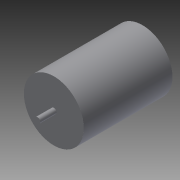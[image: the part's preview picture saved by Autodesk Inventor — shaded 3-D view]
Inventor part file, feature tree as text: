
AUTODESK INVENTOR PART (.ipt)
format: ipt  version: 2015 SP1 (Build 190203100, 203)  size: 82,944 bytes
history: native  units: in
note: dims shown in document units (in); Inventor stores cm internally (conversion verified against a paired STEP export)
features: sketch x2, revolve x1, extrude x1
ambient origin geometry x8: Origin, YZ Plane, XZ Plane, XY Plane, X Axis, Y Axis, Z Axis, Center Point
bodies: Solid1 (feature_tree)
feature tree (4):
  revolve  "Revolution1"  [1 undecoded]
  extrude  "Extrusion1"  Depth=1.88in
  sketch  "Sketch1"  dims[d0=10.2in d1=3.45in]
  sketch  "Sketch2"  dims[d2=90.0deg d3=0.625in d4=1.88in d5=0.0in]
note: 1 required parameter value undecoded (feature->parameter linkage not recoverable at this tier; creation-order binding heuristic only, values carry confidence <= 0.55)
